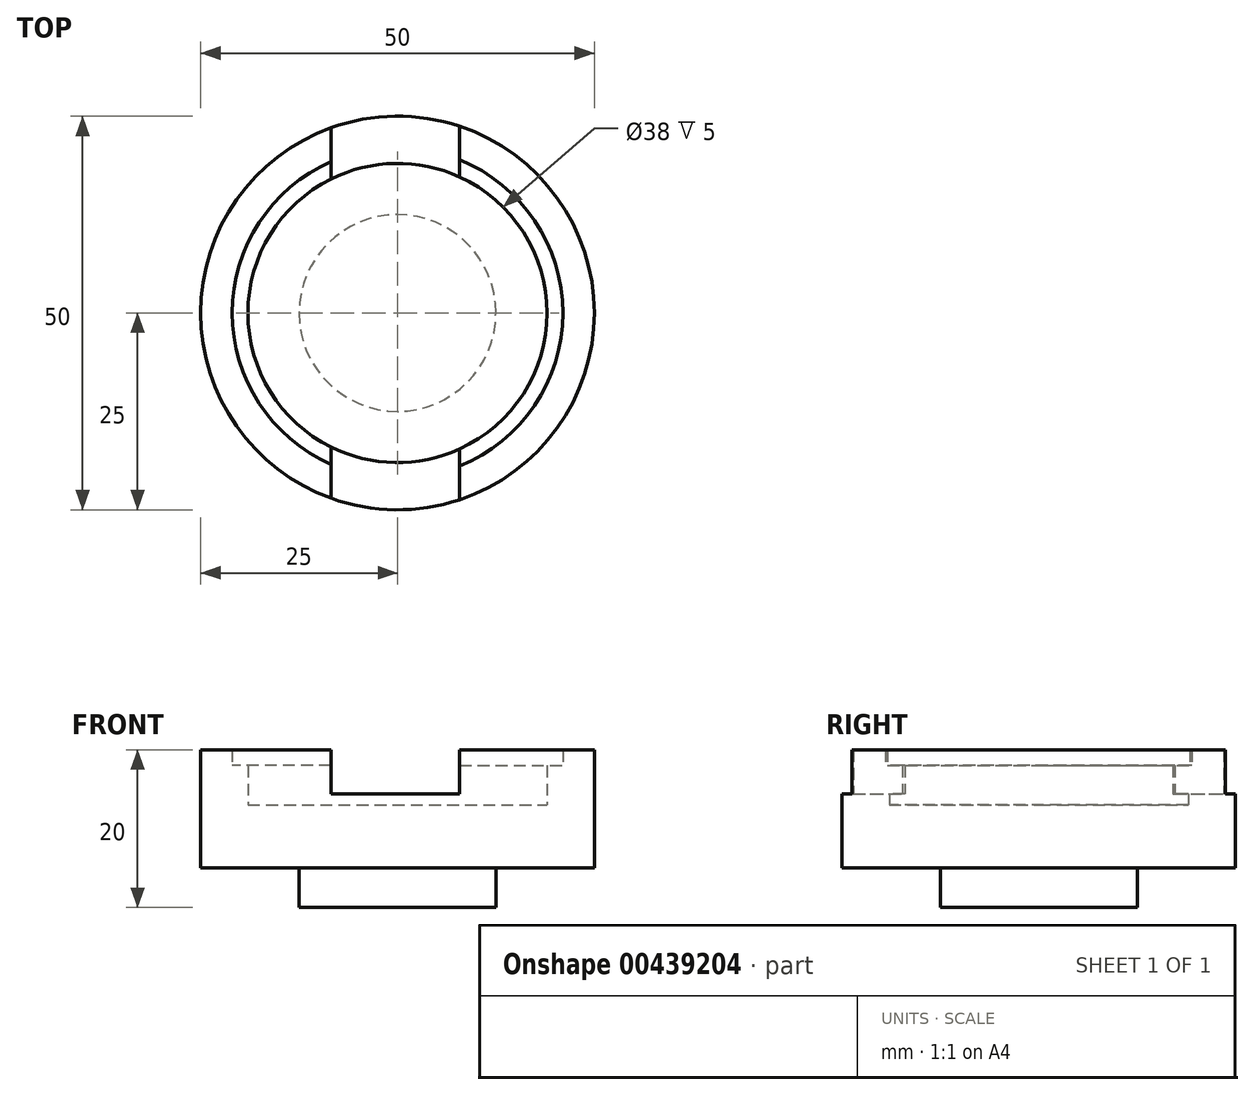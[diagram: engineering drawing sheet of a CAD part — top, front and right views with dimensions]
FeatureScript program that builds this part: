
annotation { "Feature Type Name" : "Feature", "Feature Type Description" : "" }
export const myFeature = defineFeature(function(context is Context, id is Id, definition is map)
    precondition{}
    {
        {
            var Q0;
            Q0=qCreatedBy(makeId("Front.planeOp"),FACE);
            var sketch = newSketch(context, id + "F0", { "sketchPlane" : qUnion([Q0])});
            skLineSegment(sketch, "E0", {"start": v(0, 0) * mm, "end": v(19, 0) * mm});
            skLineSegment(sketch, "E1", {"start": v(19, 0) * mm, "end": v(19, 5) * mm});
            skLineSegment(sketch, "E2", {"start": v(19, 5) * mm, "end": v(21, 5) * mm});
            skLineSegment(sketch, "E3", {"start": v(21, 5) * mm, "end": v(21, 7) * mm});
            skLineSegment(sketch, "E4", {"start": v(21, 7) * mm, "end": v(25, 7) * mm});
            skLineSegment(sketch, "E5", {"start": v(25, 7) * mm, "end": v(25, -8) * mm});
            skLineSegment(sketch, "E6", {"start": v(25, -8) * mm, "end": v(12.5, -8) * mm});
            skLineSegment(sketch, "E7", {"start": v(12.5, -8) * mm, "end": v(12.5, -13) * mm});
            skLineSegment(sketch, "E8", {"start": v(12.5, -13) * mm, "end": v(0, -13) * mm});
            skLineSegment(sketch, "E9", {"start": v(0, -13) * mm, "end": v(0, 0) * mm});
            skSolve(sketch);
        }
        {
            var Q0;
            Q0=makeQuery(id+"F0.imprint","IMPRINT",FACE,{"disambiguationData":[TD([[makeQuery(id+"F0.imprint","IMPRINT",EDGE,{"derivedFrom":sQuery(id+"F0.wireOp",EDGE,"E0")}),-1.0]])]});
            var Q1;
            Q1=sQuery(id+"F0.wireOp",EDGE,"E9");
            revolve(context, id + "F1", {"entities" : qUnion([Q0]), "axis" : qUnion([Q1]), "revolveType" : RevolveType.FULL});
        }
        {
            var Q0;
            Q0=qCreatedBy(makeId("Front.planeOp"),FACE);
            var sketch = newSketch(context, id + "F2", { "sketchPlane" : qUnion([Q0])});
            skLineSegment(sketch, "E10.bottom", {"start": v(-8.45, 8.36) * mm, "end": v(7.88, 8.36) * mm});
            skLineSegment(sketch, "E10.top", {"start": v(-8.45, 1.42) * mm, "end": v(7.88, 1.42) * mm});
            skLineSegment(sketch, "E10.left", {"start": v(-8.45, 8.36) * mm, "end": v(-8.45, 1.42) * mm});
            skLineSegment(sketch, "E10.right", {"start": v(7.88, 8.36) * mm, "end": v(7.88, 1.42) * mm});
            skSolve(sketch);
        }
        {
            var Q0;
            Q0=makeQuery(id+"F2.imprint","IMPRINT",FACE,{"disambiguationData":[TD([[makeQuery(id+"F2.imprint","IMPRINT",EDGE,{"derivedFrom":sQuery(id+"F2.wireOp",EDGE,"E10.bottom")}),-1.0]])]});
            extrude(context, id + "F3", {"entities" : qUnion([Q0]), "operationType" : NewBodyOperationType.REMOVE, "depth" : 25 * mm, "hasSecondDirection" : true, "secondDirectionOppositeDirection" : true, "secondDirectionDepth" : 25 * mm});
        }
    });
